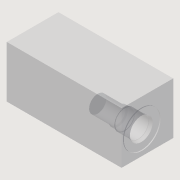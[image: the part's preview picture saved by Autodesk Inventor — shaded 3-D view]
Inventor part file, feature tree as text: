
AUTODESK INVENTOR PART (.ipt)
format: ipt  version: 2014 (Build 180170000, 170)  size: 156,672 bytes
history: native  units: mm
features: other x48, extrude x8, sketch x8
ambient origin geometry x8: Origin, YZ Plane, XZ Plane, XY Plane, X Axis, Y Axis, Z Axis, Center Point
bodies: 实体1 (feature_tree)
feature tree (64):
  extrude  "拉伸1"  Depth=32.0mm
  other  "UCS1"
  other  "UCS2"
  other  "UCS3"
  other  "UCS4"
  other  "UCS5"
  other  "UCS6"
  extrude  "拉伸2"  Depth=38.0mm
  extrude  "拉伸3"  Depth=0.79mm TaperAngle=0.0deg
  extrude  "拉伸4"  Depth=38.0mm
  extrude  "拉伸5"  Depth=38.0mm
  extrude  "拉伸6"  Depth=38.0mm
  extrude  "拉伸7"  Depth=38.0mm
  extrude  "拉伸8"  Depth=14.5mm TaperAngle=0.0deg
  sketch  "草图1"  dims[d0=45.0mm d1=0.0mm]
  sketch  "草图2"  dims[d2=0.0mm d3=0.0mm d4=0.0mm d5=0.0mm d6=0.0mm d7=0.0mm]
  sketch  "草图3"  dims[d8=0.0mm d9=0.0mm d10=0.0mm d11=0.0mm d12=0.0mm d13=0.0mm]
  sketch  "草图4"  dims[d14=0.0mm d15=0.0mm d16=0.0mm d17=0.0mm d18=0.0mm d19=0.0mm]
  sketch  "草图5"  dims[d20=0.0mm d21=0.0mm d22=0.0mm d23=0.0mm d24=0.0mm d25=0.0mm]
  sketch  "草图6"  dims[d26=0.0mm d27=0.0mm d28=0.0mm d29=0.0mm d30=0.0mm d31=0.0mm]
  sketch  "草图7"  dims[d32=0.0mm d33=0.0mm d34=0.0mm d35=0.0mm d36=0.0mm d37=0.0mm d38=32.0mm]
  sketch  "草图8"  dims[d39=18.0mm d40=20.0mm d41=0.79mm d42=0.0mm d43=19.85mm d44=2.6mm d45=-2.617994mm d46=2.6mm d47=-7.853982mm d48=18.0mm d49=14.5mm d50=0.0mm d51=16.5mm d52=20.0mm d53=0.0mm d54=20.0mm d55=-5.235988mm d56=15.0mm d57=38.0mm d58=0.0mm]
  other  "UCS1: YZ 平面"
  other  "UCS1: XZ 平面"
  other  "UCS1: XY 平面"
  other  "UCS1: X 轴"
  other  "UCS1: Y 轴"
  other  "UCS1: Z 轴"
  other  "UCS1: 原点"
  other  "UCS2: YZ 平面"
  other  "UCS2: XZ 平面"
  other  "UCS2: XY 平面"
  other  "UCS2: X 轴"
  other  "UCS2: Y 轴"
  other  "UCS2: Z 轴"
  other  "UCS2: 原点"
  other  "UCS3: YZ 平面"
  other  "UCS3: XZ 平面"
  other  "UCS3: XY 平面"
  other  "UCS3: X 轴"
  other  "UCS3: Y 轴"
  other  "UCS3: Z 轴"
  other  "UCS3: 原点"
  other  "UCS4: YZ 平面"
  other  "UCS4: XZ 平面"
  other  "UCS4: XY 平面"
  other  "UCS4: X 轴"
  other  "UCS4: Y 轴"
  other  "UCS4: Z 轴"
  other  "UCS4: 原点"
  other  "UCS5: YZ 平面"
  other  "UCS5: XZ 平面"
  other  "UCS5: XY 平面"
  other  "UCS5: X 轴"
  other  "UCS5: Y 轴"
  other  "UCS5: Z 轴"
  other  "UCS5: 原点"
  other  "UCS6: YZ 平面"
  other  "UCS6: XZ 平面"
  other  "UCS6: XY 平面"
  other  "UCS6: X 轴"
  other  "UCS6: Y 轴"
  other  "UCS6: Z 轴"
  other  "UCS6: 原点"
